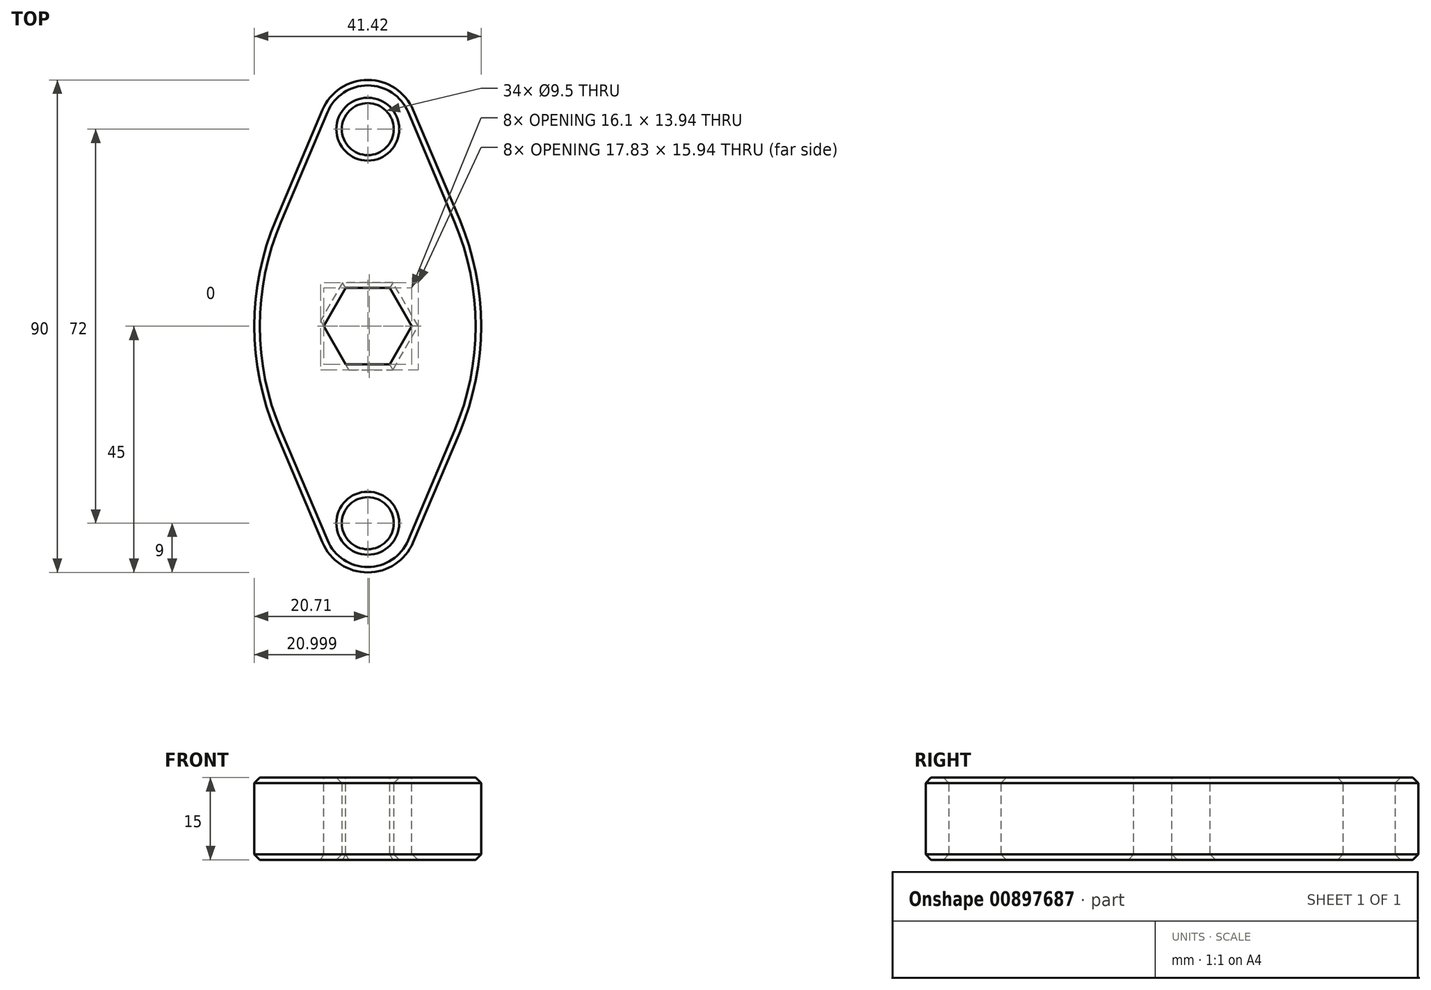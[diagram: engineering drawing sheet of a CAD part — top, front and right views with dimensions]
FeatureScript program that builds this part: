
annotation { "Feature Type Name" : "Feature", "Feature Type Description" : "" }
export const myFeature = defineFeature(function(context is Context, id is Id, definition is map)
    precondition{}
    {
        {
            var Q0;
            Q0=qCreatedBy(makeId("Top.planeOp"),FACE);
            var sketch = newSketch(context, id + "F0", { "sketchPlane" : qUnion([Q0])});
            skLineSegment(sketch, "E0", {"start": v(0, 83.57) * mm, "end": v(0, -89.6) * mm, "construction": true});
            skLineSegment(sketch, "E1", {"start": v(81.05, 0) * mm, "end": v(-79.37, 0) * mm, "construction": true});
            skArc(sketch, "E2", {"start": v(8.29, 39.5) * mm, "mid": v(0, 45) * mm, "end": v(-8.29, 39.5) * mm});
            skLineSegment(sketch, "E3", {"start": v(-26.39, 36) * mm, "end": v(35.06, 36) * mm, "construction": true});
            skArc(sketch, "E4.MirrorCS", {"start": v(8.29, -39.5) * mm, "mid": v(0, -45) * mm, "end": v(-8.29, -39.5) * mm});
            skLineSegment(sketch, "E5", {"start": v(-8.29, 39.5) * mm, "end": v(-25, 0) * mm});
            skLineSegment(sketch, "E6.MirrorCS", {"start": v(8.29, 39.5) * mm, "end": v(25, 0) * mm});
            skPoint(sketch, "E7.orphan", {"position": v(-4.96, 47.37) * mm});
            skPoint(sketch, "E8.orphan", {"position": v(4.96, 47.37) * mm});
            skLineSegment(sketch, "E9.MirrorCS", {"start": v(-8.29, -39.5) * mm, "end": v(-25, 0) * mm});
            skLineSegment(sketch, "E10.MirrorCS", {"start": v(8.29, -39.5) * mm, "end": v(25, 0) * mm});
            skPoint(sketch, "E11.end.orphan", {"position": v(-10, 0) * mm});
            skPoint(sketch, "E11.start.orphan", {"position": v(-9, 36) * mm});
            skPoint(sketch, "E12.end.orphan", {"position": v(10, 0) * mm});
            skPoint(sketch, "E13.orphan", {"position": v(9, 36) * mm});
            skPoint(sketch, "E14.MirrorCS.start.orphan", {"position": v(-9, -36) * mm});
            skPoint(sketch, "E15.orphan", {"position": v(9, -36) * mm});
            skLineSegment(sketch, "E16", {"start": v(-34.58, 46.77) * mm, "end": v(38.96, 46.77) * mm, "construction": true});
            skLineSegment(sketch, "E17.MirrorCS", {"start": v(-34.58, -46.78) * mm, "end": v(38.96, -46.77) * mm, "construction": true});
            skCircle(sketch, "E18", {"center": v(0, 36) * mm, "radius": 11.1 * mm, "construction": true});
            skCircle(sketch, "E19", {"center": v(0, 36) * mm, "radius": 4.75 * mm});
            skCircle(sketch, "E20.MirrorC", {"center": v(0, -36) * mm, "radius": 4.75 * mm});
            skSolve(sketch);
        }
        {
            var Q0;
            Q0=makeQuery(id+"F0.imprint","IMPRINT",FACE,{"disambiguationData":[TD([[makeQuery(id+"F0.imprint","IMPRINT",EDGE,{"derivedFrom":sQuery(id+"F0.wireOp",EDGE,"E2")}),1.0]])]});
            extrude(context, id + "F1", {"entities" : qUnion([Q0]), "endBound" : BoundingType.SYMMETRIC, "depth" : 15 * mm, "offsetDistance" : 25 * mm});
        }
        {
            var Q0;
            Q0=makeQuery(id+"F1.opExtrude","SWEPT_EDGE",EDGE,{"disambiguationData":[OSD([sQuery(id+"F0.wireOp",EDGE,"E5"),sQuery(id+"F0.wireOp",EDGE,"E9.MirrorCS")])]});
            var Q1;
            Q1=makeQuery(id+"F1.opExtrude","SWEPT_EDGE",EDGE,{"disambiguationData":[OSD([sQuery(id+"F0.wireOp",EDGE,"E6.MirrorCS"),sQuery(id+"F0.wireOp",EDGE,"E10.MirrorCS")])]});
            fillet(context, id + "F2", {"entities" : qUnion([Q0, Q1]), "radius" : 50 * mm, "tangentPropagation" : true, "allowEdgeOverflow" : false});
        }
        {
            var Q0;
            Q0=makeQuery(id+"F1.opExtrude","CAP_EDGE",EDGE,{"disambiguationData":[OSD([sQuery(id+"F0.wireOp",EDGE,"E2")])],"isStart":false});
            var Q1;
            Q1=makeQuery(id+"F1.opExtrude","CAP_EDGE",EDGE,{"disambiguationData":[OSD([sQuery(id+"F0.wireOp",EDGE,"E2")])],"isStart":true});
            var Q2;
            Q2=makeQuery(id+"F1.opExtrude","CAP_EDGE",EDGE,{"disambiguationData":[OSD([sQuery(id+"F0.wireOp",EDGE,"E9.MirrorCS")])],"isStart":false});
            var Q3;
            Q3=makeQuery(id+"F1.opExtrude","CAP_EDGE",EDGE,{"disambiguationData":[OSD([sQuery(id+"F0.wireOp",EDGE,"E9.MirrorCS")])],"isStart":true});
            chamfer(context, id + "F3", {"entities" : qUnion([Q0, Q1, Q2, Q3]), "width" : 1 * mm, "tangentPropagation" : true});
        }
        {
            var Q0;
            Q0=makeQuery(id+"F1.opExtrude","CAP_FACE",FACE,{"disambiguationData":[OSD([sQuery(id+"F0.wireOp",EDGE,"E2"),sQuery(id+"F0.wireOp",EDGE,"E4.MirrorCS"),sQuery(id+"F0.wireOp",EDGE,"E5"),sQuery(id+"F0.wireOp",EDGE,"E6.MirrorCS"),sQuery(id+"F0.wireOp",EDGE,"E9.MirrorCS"),sQuery(id+"F0.wireOp",EDGE,"E10.MirrorCS"),sQuery(id+"F0.wireOp",EDGE,"E19"),sQuery(id+"F0.wireOp",EDGE,"E20.MirrorC")])],"isStart":false});
            var sketch = newSketch(context, id + "F4", { "sketchPlane" : qUnion([Q0])});
            skLineSegment(sketch, "E21", {"start": v(-10.5, 0) * mm, "end": v(11.12, 0) * mm, "construction": true});
            skLineSegment(sketch, "E22", {"start": v(0, 0) * mm, "end": v(-5.1, 8.84) * mm, "construction": true});
            skLineSegment(sketch, "E23.MirrorCS", {"start": v(0, 0) * mm, "end": v(5.1, 8.84) * mm, "construction": true});
            skLineSegment(sketch, "E24.MirrorCS", {"start": v(0, 0) * mm, "end": v(-5.1, -8.84) * mm, "construction": true});
            skLineSegment(sketch, "E25.MirrorCS", {"start": v(0, 0) * mm, "end": v(5.1, -8.84) * mm, "construction": true});
            skLineSegment(sketch, "E26", {"start": v(-8.05, 0) * mm, "end": v(-4.03, 6.97) * mm});
            skLineSegment(sketch, "E27", {"start": v(-4.02, 6.97) * mm, "end": v(4.02, 6.97) * mm});
            skLineSegment(sketch, "E28", {"start": v(4.02, 6.97) * mm, "end": v(8.05, 0) * mm});
            skLineSegment(sketch, "E29", {"start": v(8.05, 0) * mm, "end": v(4.03, -6.97) * mm});
            skLineSegment(sketch, "E30", {"start": v(4.03, -6.97) * mm, "end": v(-4.03, -6.97) * mm});
            skLineSegment(sketch, "E31", {"start": v(-4.02, -6.97) * mm, "end": v(-8.05, 0) * mm});
            skSolve(sketch);
        }
        {
            var Q0;
            Q0=qSketchRegion(id+"F4",true);
            extrude(context, id + "F5", {"entities" : qUnion([Q0]), "operationType" : NewBodyOperationType.REMOVE, "oppositeDirection" : true, "depth" : 25 * mm, "offsetDistance" : 25 * mm});
        }
        {
            var Q0;
            Q0=makeQuery(id+"F1.opExtrude","CAP_EDGE",EDGE,{"disambiguationData":[OSD([sQuery(id+"F0.wireOp",EDGE,"E19")])],"isStart":false});
            var Q1;
            Q1=makeQuery(id+"F1.opExtrude","CAP_EDGE",EDGE,{"disambiguationData":[OSD([sQuery(id+"F0.wireOp",EDGE,"E19")])],"isStart":true});
            var Q2;
            Q2=makeQuery(id+"F1.opExtrude","CAP_EDGE",EDGE,{"disambiguationData":[OSD([sQuery(id+"F0.wireOp",EDGE,"E20.MirrorC")])],"isStart":false});
            var Q3;
            Q3=makeQuery(id+"F1.opExtrude","CAP_EDGE",EDGE,{"disambiguationData":[OSD([sQuery(id+"F0.wireOp",EDGE,"E20.MirrorC")])],"isStart":true});
            var Q4;
            Q4=makeQuery(id+"F5.boolean.opBoolean","COPY",EDGE,{"derivedFrom":makeQuery(id+"F5.opExtrude","CAP_EDGE",EDGE,{"disambiguationData":[OSD([sQuery(id+"F4.wireOp",EDGE,"E30")])],"isStart":true})});
            var Q5;
            Q5=makeQuery(id+"F5.boolean.opBoolean","COPY",EDGE,{"derivedFrom":makeQuery(id+"F5.opExtrude","CAP_EDGE",EDGE,{"disambiguationData":[OSD([sQuery(id+"F4.wireOp",EDGE,"E31")])],"isStart":true})});
            var Q6;
            Q6=makeQuery(id+"F5.boolean.opBoolean","COPY",EDGE,{"derivedFrom":makeQuery(id+"F5.opExtrude","CAP_EDGE",EDGE,{"disambiguationData":[OSD([sQuery(id+"F4.wireOp",EDGE,"E26")])],"isStart":true})});
            var Q7;
            Q7=makeQuery(id+"F5.boolean.opBoolean","COPY",EDGE,{"derivedFrom":makeQuery(id+"F5.opExtrude","CAP_EDGE",EDGE,{"disambiguationData":[OSD([sQuery(id+"F4.wireOp",EDGE,"E27")])],"isStart":true})});
            var Q8;
            Q8=makeQuery(id+"F5.boolean.opBoolean","COPY",EDGE,{"derivedFrom":makeQuery(id+"F5.opExtrude","CAP_EDGE",EDGE,{"disambiguationData":[OSD([sQuery(id+"F4.wireOp",EDGE,"E28")])],"isStart":true})});
            var Q9;
            Q9=makeQuery(id+"F5.boolean.opBoolean","COPY",EDGE,{"derivedFrom":makeQuery(id+"F5.opExtrude","CAP_EDGE",EDGE,{"disambiguationData":[OSD([sQuery(id+"F4.wireOp",EDGE,"E29")])],"isStart":true})});
            var Q10;
            Q10=makeQuery(id+"F5.boolean.opBoolean","INTERSECT",EDGE,{"derivedFrom":[makeQuery(id+"F1.opExtrude","CAP_FACE",FACE,{"disambiguationData":[OSD([sQuery(id+"F0.wireOp",EDGE,"E2"),sQuery(id+"F0.wireOp",EDGE,"E4.MirrorCS"),sQuery(id+"F0.wireOp",EDGE,"E5"),sQuery(id+"F0.wireOp",EDGE,"E6.MirrorCS"),sQuery(id+"F0.wireOp",EDGE,"E9.MirrorCS"),sQuery(id+"F0.wireOp",EDGE,"E10.MirrorCS"),sQuery(id+"F0.wireOp",EDGE,"E19"),sQuery(id+"F0.wireOp",EDGE,"E20.MirrorC")])],"isStart":true}),makeQuery(id+"F5.opExtrude","SWEPT_FACE",FACE,{"disambiguationData":[OSD([sQuery(id+"F4.wireOp",EDGE,"E30")])]})]});
            var Q11;
            Q11=makeQuery(id+"F5.boolean.opBoolean","INTERSECT",EDGE,{"derivedFrom":[makeQuery(id+"F1.opExtrude","CAP_FACE",FACE,{"disambiguationData":[OSD([sQuery(id+"F0.wireOp",EDGE,"E2"),sQuery(id+"F0.wireOp",EDGE,"E4.MirrorCS"),sQuery(id+"F0.wireOp",EDGE,"E5"),sQuery(id+"F0.wireOp",EDGE,"E6.MirrorCS"),sQuery(id+"F0.wireOp",EDGE,"E9.MirrorCS"),sQuery(id+"F0.wireOp",EDGE,"E10.MirrorCS"),sQuery(id+"F0.wireOp",EDGE,"E19"),sQuery(id+"F0.wireOp",EDGE,"E20.MirrorC")])],"isStart":true}),makeQuery(id+"F5.opExtrude","SWEPT_FACE",FACE,{"disambiguationData":[OSD([sQuery(id+"F4.wireOp",EDGE,"E29")])]})]});
            var Q12;
            Q12=makeQuery(id+"F5.boolean.opBoolean","INTERSECT",EDGE,{"derivedFrom":[makeQuery(id+"F1.opExtrude","CAP_FACE",FACE,{"disambiguationData":[OSD([sQuery(id+"F0.wireOp",EDGE,"E2"),sQuery(id+"F0.wireOp",EDGE,"E4.MirrorCS"),sQuery(id+"F0.wireOp",EDGE,"E5"),sQuery(id+"F0.wireOp",EDGE,"E6.MirrorCS"),sQuery(id+"F0.wireOp",EDGE,"E9.MirrorCS"),sQuery(id+"F0.wireOp",EDGE,"E10.MirrorCS"),sQuery(id+"F0.wireOp",EDGE,"E19"),sQuery(id+"F0.wireOp",EDGE,"E20.MirrorC")])],"isStart":true}),makeQuery(id+"F5.opExtrude","SWEPT_FACE",FACE,{"disambiguationData":[OSD([sQuery(id+"F4.wireOp",EDGE,"E28")])]})]});
            var Q13;
            Q13=makeQuery(id+"F5.boolean.opBoolean","INTERSECT",EDGE,{"derivedFrom":[makeQuery(id+"F1.opExtrude","CAP_FACE",FACE,{"disambiguationData":[OSD([sQuery(id+"F0.wireOp",EDGE,"E2"),sQuery(id+"F0.wireOp",EDGE,"E4.MirrorCS"),sQuery(id+"F0.wireOp",EDGE,"E5"),sQuery(id+"F0.wireOp",EDGE,"E6.MirrorCS"),sQuery(id+"F0.wireOp",EDGE,"E9.MirrorCS"),sQuery(id+"F0.wireOp",EDGE,"E10.MirrorCS"),sQuery(id+"F0.wireOp",EDGE,"E19"),sQuery(id+"F0.wireOp",EDGE,"E20.MirrorC")])],"isStart":true}),makeQuery(id+"F5.opExtrude","SWEPT_FACE",FACE,{"disambiguationData":[OSD([sQuery(id+"F4.wireOp",EDGE,"E27")])]})]});
            var Q14;
            Q14=makeQuery(id+"F5.boolean.opBoolean","INTERSECT",EDGE,{"derivedFrom":[makeQuery(id+"F1.opExtrude","CAP_FACE",FACE,{"disambiguationData":[OSD([sQuery(id+"F0.wireOp",EDGE,"E2"),sQuery(id+"F0.wireOp",EDGE,"E4.MirrorCS"),sQuery(id+"F0.wireOp",EDGE,"E5"),sQuery(id+"F0.wireOp",EDGE,"E6.MirrorCS"),sQuery(id+"F0.wireOp",EDGE,"E9.MirrorCS"),sQuery(id+"F0.wireOp",EDGE,"E10.MirrorCS"),sQuery(id+"F0.wireOp",EDGE,"E19"),sQuery(id+"F0.wireOp",EDGE,"E20.MirrorC")])],"isStart":true}),makeQuery(id+"F5.opExtrude","SWEPT_FACE",FACE,{"disambiguationData":[OSD([sQuery(id+"F4.wireOp",EDGE,"E26")])]})]});
            chamfer(context, id + "F6", {"entities" : qUnion([Q0, Q1, Q2, Q3, Q4, Q5, Q6, Q7, Q8, Q9, Q10, Q11, Q12, Q13, Q14]), "width" : 1 * mm, "tangentPropagation" : true});
        }
    });
